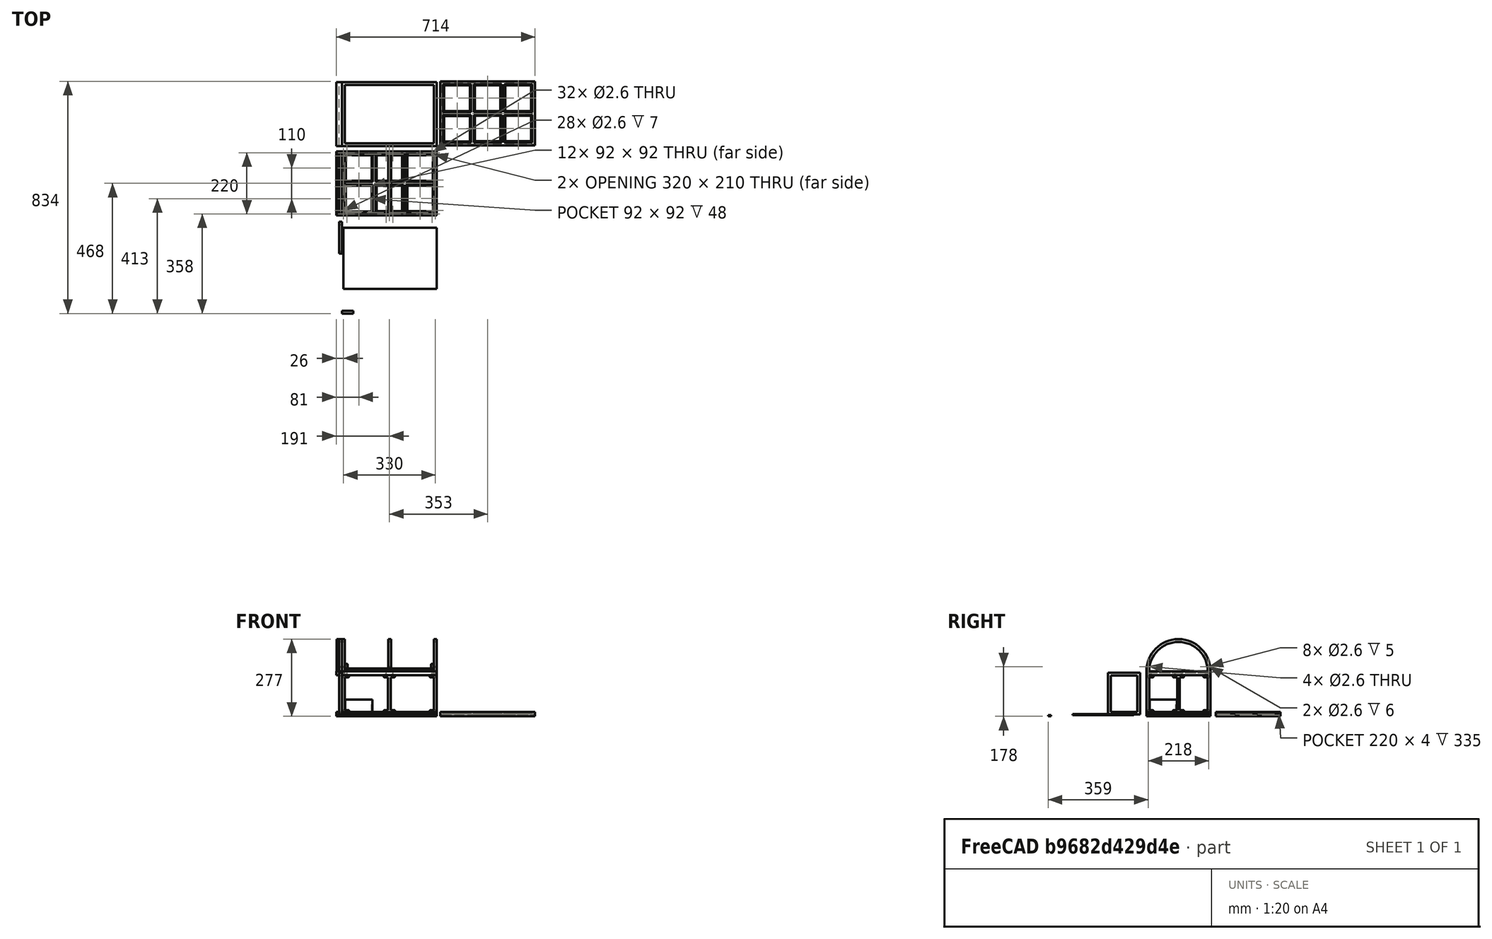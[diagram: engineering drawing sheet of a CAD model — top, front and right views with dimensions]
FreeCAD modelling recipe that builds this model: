
FCSTD DOCUMENT  (FreeCAD 0.18R4 (GitTag))
Label: 3DMODEL
License: All rights reserved
LicenseURL: http://en.wikipedia.org/wiki/All_rights_reserved
objects: Part::Box×95, Part::Cut×92, Part::Cylinder×85, Part::MultiFuse×18, App::MeasureDistance×12, Part::Fillet×12, Mesh::Feature×2
note: 302 computed .brp shape members not serialized (recipe doc carries the construction recipe); baked Part::Feature solids carry a one-line shape summary decoded from their .brp

FEATURE [Part::Box] Box  label="base1"
  AttacherType = Attacher::AttachEngine3D
  Height = 15
  Length = 340
  Width = 10
FEATURE [Part::Box] Box001  label="base2"
  AttacherType = Attacher::AttachEngine3D
  Height = 15
  Length = 340
  Placement = pos=(0,220,0) rot=(0,0,1;0rad)
  Width = 10
FEATURE [Part::Box] Box002  label="ancho"
  AttacherType = Attacher::AttachEngine3D
  Height = 15
  Length = 10
  Placement = pos=(0,10,0) rot=(0,0,1;0rad)
  Width = 210
FEATURE [Part::Box] Box003  label="ancho001"
  AttacherType = Attacher::AttachEngine3D
  Height = 15
  Length = 10
  Placement = pos=(330,10,0) rot=(0,0,1;0rad)
  Width = 210
FEATURE [Part::Box] Box004  label="cajita1"
  AttacherType = Attacher::AttachEngine3D
  Height = 2
  Length = 320
  Placement = pos=(10,10,8) rot=(0,0,1;0rad)
  Width = 210
FEATURE [Part::Box] Box006  label="base003"
  AttacherType = Attacher::AttachEngine3D
  Height = 7
  Length = 340
  Placement = pos=(0,110,8) rot=(0,0,1;0rad)
  Width = 10
FEATURE [Part::Box] Box011  label="ancho002"
  AttacherType = Attacher::AttachEngine3D
  Height = 7
  Length = 10
  Placement = pos=(110,10,8) rot=(0,0,1;0rad)
  Width = 210
FEATURE [Part::Box] Box012  label="ancho003"
  AttacherType = Attacher::AttachEngine3D
  Height = 7
  Length = 10
  Placement = pos=(220,10,8) rot=(0,0,1;0rad)
  Width = 210
FEATURE [Part::Box] Box013  label="cajita007"
  AttacherType = Attacher::AttachEngine3D
  Height = 24
  Length = 92
  Placement = pos=(14,14,0) rot=(0,0,1;0rad)
  Width = 92
FEATURE [Part::MultiFuse] Fusion  label="base"
  Shapes = -> [Box011,Box012,Box006,Box003,Box002,Box001,Box]
FEATURE [Part::Box] Box015  label="cajita009"
  AttacherType = Attacher::AttachEngine3D
  Height = 4
  Length = 335
  Placement = pos=(5,5,4) rot=(0,0,1;0rad)
  Width = 220
FEATURE [Part::Box] Box016  label="plancha"
  AttacherType = Attacher::AttachEngine3D
  Height = 4
  Length = 335
  Placement = pos=(5,-265,4) rot=(0,0,1;0rad)
  Width = 220
FEATURE [Part::Cut] Cut
  Base = -> Fusion
  Tool = -> Box015
FEATURE [Part::MultiFuse] Fusion001
  Shapes = -> [Cut,Box004]
FEATURE [Part::Cut] Cut001
  Base = -> Fusion001
  Tool = -> Box013
FEATURE [Part::Box] Box017  label="cajita011"
  AttacherType = Attacher::AttachEngine3D
  Height = 24
  Length = 92
  Placement = pos=(124,15,0) rot=(0,0,1;0rad)
  Width = 92
FEATURE [Part::Cut] Cut002
  Base = -> Cut001
  Tool = -> Box017
FEATURE [Part::Box] Box018  label="cajita012"
  AttacherType = Attacher::AttachEngine3D
  Height = 24
  Length = 92
  Placement = pos=(234,15,0) rot=(0,0,1;0rad)
  Width = 92
FEATURE [Part::Cut] Cut003
  Base = -> Cut002
  Tool = -> Box018
FEATURE [Part::Box] Box019  label="cajita013"
  AttacherType = Attacher::AttachEngine3D
  Height = 24
  Length = 92
  Placement = pos=(234,124,0) rot=(0,0,1;0rad)
  Width = 92
FEATURE [Part::Cut] Cut004
  Base = -> Cut003
  Tool = -> Box019
FEATURE [Part::Box] Box020  label="cajita014"
  AttacherType = Attacher::AttachEngine3D
  Height = 24
  Length = 92
  Placement = pos=(124,124,0) rot=(0,0,1;0rad)
  Width = 92
FEATURE [Part::Cut] Cut005
  Base = -> Cut004
  Tool = -> Box020
FEATURE [Part::Box] Box021  label="cajita015"
  AttacherType = Attacher::AttachEngine3D
  Height = 24
  Length = 92
  Placement = pos=(14,124,0) rot=(0,0,1;0rad)
  Width = 92
FEATURE [Part::Cut] Cut006  label="base004"
  Base = -> Cut005
  Tool = -> Box021
FEATURE [Part::Box] Box022  label="Cubo"
  AttacherType = Attacher::AttachEngine3D
  Height = 50
  Length = 98
  Placement = pos=(11,11,0) rot=(0,0,1;0rad)
  Width = 98
FEATURE [Part::Box] Box023  label="Cubo001"
  AttacherType = Attacher::AttachEngine3D
  Height = 80
  Length = 92
  Placement = pos=(14,14,2) rot=(0,0,1;0rad)
  Width = 92
FEATURE [Part::Cut] Cut007  label="cajita"
  Base = -> Box022
  Placement = pos=(0,0,10) rot=(0,0,1;0rad)
  Tool = -> Box023
FEATURE [App::MeasureDistance] Distance  label="Distance: 340,00 mm"
  Distance = 340
  P1 = (0,230,15)
  P2 = (340,229.956,15)
FEATURE [Part::Box] Box024  label="Cubo002"
  AttacherType = Attacher::AttachEngine3D
  Height = 15
  Length = 10
  Placement = pos=(0,259,0) rot=(0,0,1;0rad)
  Width = 210
FEATURE [App::MeasureDistance] Distance001  label="Distance: 230,00 mm"
  Distance = 230
  P1 = (340,230,15)
  P2 = (340,0,15)
FEATURE [Part::Box] Box025  label="base005"
  AttacherType = Attacher::AttachEngine3D
  Height = 15
  Length = 340
  Width = 10
FEATURE [Part::Box] Box026  label="base006"
  AttacherType = Attacher::AttachEngine3D
  Height = 15
  Length = 340
  Placement = pos=(0,220,0) rot=(0,0,1;0rad)
  Width = 10
FEATURE [Part::Box] Box027  label="ancho004"
  AttacherType = Attacher::AttachEngine3D
  Height = 15
  Length = 10
  Placement = pos=(330,10,0) rot=(0,0,1;0rad)
  Width = 210
FEATURE [Part::Box] Box028  label="base007"
  AttacherType = Attacher::AttachEngine3D
  Height = 7
  Length = 340
  Placement = pos=(0,110,8) rot=(0,0,1;0rad)
  Width = 10
FEATURE [Part::Box] Box029  label="ancho005"
  AttacherType = Attacher::AttachEngine3D
  Height = 7
  Length = 10
  Placement = pos=(110,10,8) rot=(0,0,1;0rad)
  Width = 210
FEATURE [Part::Box] Box030  label="cajita016"
  AttacherType = Attacher::AttachEngine3D
  Height = 2
  Length = 320
  Placement = pos=(10,10,8) rot=(0,0,1;0rad)
  Width = 210
FEATURE [Part::Box] Box031  label="ancho006"
  AttacherType = Attacher::AttachEngine3D
  Height = 7
  Length = 10
  Placement = pos=(220,10,8) rot=(0,0,1;0rad)
  Width = 210
FEATURE [Part::Box] Box032  label="cajita017"
  AttacherType = Attacher::AttachEngine3D
  Height = 24
  Length = 92
  Placement = pos=(14,14,0) rot=(0,0,1;0rad)
  Width = 92
FEATURE [Part::Box] Box033  label="ancho007"
  AttacherType = Attacher::AttachEngine3D
  Height = 15
  Length = 10
  Placement = pos=(0,10,0) rot=(0,0,1;0rad)
  Width = 210
FEATURE [Part::MultiFuse] Fusion003  label="base009"
  Shapes = -> [Box029,Box031,Box028,Box027,Box033,Box026,Box025]
FEATURE [Part::Box] Box034  label="cajita018"
  AttacherType = Attacher::AttachEngine3D
  Height = 24
  Length = 92
  Placement = pos=(124,124,0) rot=(0,0,1;0rad)
  Width = 92
FEATURE [Part::Box] Box035  label="cajita019"
  AttacherType = Attacher::AttachEngine3D
  Height = 24
  Length = 92
  Placement = pos=(124,15,0) rot=(0,0,1;0rad)
  Width = 92
FEATURE [Part::Box] Box036  label="cajita020"
  AttacherType = Attacher::AttachEngine3D
  Height = 24
  Length = 92
  Placement = pos=(234,124,0) rot=(0,0,1;0rad)
  Width = 92
FEATURE [Part::Box] Box037  label="cajita021"
  AttacherType = Attacher::AttachEngine3D
  Height = 24
  Length = 92
  Placement = pos=(234,15,0) rot=(0,0,1;0rad)
  Width = 92
FEATURE [Part::Box] Box039  label="cajita023"
  AttacherType = Attacher::AttachEngine3D
  Height = 4
  Length = 335
  Placement = pos=(5,5,4) rot=(0,0,1;0rad)
  Width = 220
FEATURE [Part::Cut] Cut012
  Base = -> Fusion003
  Tool = -> Box039
FEATURE [Part::MultiFuse] Fusion002
  Shapes = -> [Cut012,Box030]
FEATURE [Part::Cut] Cut008
  Base = -> Fusion002
  Tool = -> Box032
FEATURE [Part::Cut] Cut009
  Base = -> Cut008
  Tool = -> Box035
FEATURE [Part::Cut] Cut014
  Base = -> Cut009
  Tool = -> Box037
FEATURE [Part::Cut] Cut010
  Base = -> Cut014
  Tool = -> Box036
FEATURE [Part::Cut] Cut011
  Base = -> Cut010
  Tool = -> Box034
FEATURE [Part::Box] Box038  label="cajita022"
  AttacherType = Attacher::AttachEngine3D
  Height = 24
  Length = 92
  Placement = pos=(14,124,0) rot=(0,0,1;0rad)
  Width = 92
FEATURE [Part::Cut] Cut013  label="BaseOriginal"
  Base = -> Cut011
  Placement = pos=(353,251,0) rot=(0,0,1;0rad)
  Tool = -> Box038
FEATURE [Part::Box] Box040  label="Cubo003"
  AttacherType = Attacher::AttachEngine3D
  Height = 15
  Length = 340
  Placement = pos=(0,249,0) rot=(0,0,1;0rad)
  Width = 10
FEATURE [Part::Box] Box041  label="Cubo004"
  AttacherType = Attacher::AttachEngine3D
  Height = 15
  Length = 10
  Placement = pos=(330,259,0) rot=(0,0,1;0rad)
  Width = 210
FEATURE [Part::Box] Box042  label="Cubo005"
  AttacherType = Attacher::AttachEngine3D
  Height = 15
  Length = 340
  Placement = pos=(0,469,0) rot=(0,0,1;0rad)
  Width = 10
FEATURE [Part::MultiFuse] Fusion004  label="techo"
  Shapes = -> [Box042,Box041,Box040,Box024]
FEATURE [App::MeasureDistance] Distance002  label="Distance: 340,00 mm001"
  Distance = 340
  P1 = (0,479,15)
  P2 = (340,479,15)
FEATURE [App::MeasureDistance] Distance003  label="Distance: 230,00 mm001"
  Distance = 230
  P1 = (339.999,479,15)
  P2 = (340,249,15)
FEATURE [App::MeasureDistance] Distance004  label="Distance: 100,00 mm"
  Distance = 100
  P1 = (330,219.999,15)
  P2 = (230,219.997,15)
FEATURE [Part::Box] Box043  label="Cubo006"
  AttacherType = Attacher::AttachEngine3D
  Height = 5
  Length = 21
  Placement = pos=(-21,0,0) rot=(0,0,1;0rad)
  Width = 230
FEATURE [Part::Box] Box044  label="Cubo007"
  AttacherType = Attacher::AttachEngine3D
  Height = 10
  Length = 10
  Placement = pos=(-21,0,5) rot=(0,0,1;0rad)
  Width = 230
FEATURE [Part::Box] Box045  label="Cubo008"
  AttacherType = Attacher::AttachEngine3D
  Height = 5
  Length = 21
  Placement = pos=(-21,249,10) rot=(0,0,1;0rad)
  Width = 230
FEATURE [Part::Box] Box046  label="Cubo009"
  AttacherType = Attacher::AttachEngine3D
  Height = 10
  Length = 10
  Placement = pos=(-21,249,0) rot=(0,0,1;0rad)
  Width = 230
FEATURE [App::MeasureDistance] Distance005  label="Distance: 11,00 mm"
  Distance = 11
  P1 = (0,0,15)
  P2 = (-11,0,15)
FEATURE [Part::Box] Box048  label="Cubo011"
  AttacherType = Attacher::AttachEngine3D
  Height = 130
  Length = 10
  Placement = pos=(-37,220,15) rot=(0,0,1;0rad)
  Width = 10
FEATURE [Part::Box] Box049  label="Cubo012"
  AttacherType = Attacher::AttachEngine3D
  Height = 130
  Length = 10
  Placement = pos=(-37,115,15) rot=(0,0,1;0rad)
  Width = 10
FEATURE [Part::Box] Box050  label="Cubo013"
  AttacherType = Attacher::AttachEngine3D
  Height = 10
  Length = 10
  Placement = pos=(-37,115,145) rot=(0,0,1;0rad)
  Width = 115
FEATURE [Part::Box] Box051  label="Cubo014"
  AttacherType = Attacher::AttachEngine3D
  Height = 10
  Length = 10
  Placement = pos=(-37,115,5) rot=(0,0,1;0rad)
  Width = 115
FEATURE [Part::MultiFuse] Fusion005
  Placement = pos=(0,-249,147) rot=(0,0,1;0rad)
  Shapes = -> [Box045,Box046,Fusion004]
FEATURE [Part::Box] Box052  label="Cubo015"
  AttacherType = Attacher::AttachEngine3D
  Height = 15
  Length = 340
  Placement = pos=(0,249,0) rot=(0,0,1;0rad)
  Width = 10
FEATURE [Part::Box] Box053  label="Cubo016"
  AttacherType = Attacher::AttachEngine3D
  Height = 15
  Length = 10
  Placement = pos=(330,259,0) rot=(0,0,1;0rad)
  Width = 210
FEATURE [Part::Box] Box054  label="Cubo017"
  AttacherType = Attacher::AttachEngine3D
  Height = 15
  Length = 10
  Placement = pos=(0,259,0) rot=(0,0,1;0rad)
  Width = 210
FEATURE [Part::Box] Box055  label="Cubo018"
  AttacherType = Attacher::AttachEngine3D
  Height = 15
  Length = 340
  Placement = pos=(0,469,0) rot=(0,0,1;0rad)
  Width = 10
FEATURE [Part::MultiFuse] Fusion006  label="techo001"
  Shapes = -> [Box055,Box053,Box052,Box054]
FEATURE [Part::Box] Box056  label="Cubo019"
  AttacherType = Attacher::AttachEngine3D
  Height = 5
  Length = 21
  Placement = pos=(-21,249,10) rot=(0,0,1;0rad)
  Width = 230
FEATURE [Part::Box] Box057  label="Cubo020"
  AttacherType = Attacher::AttachEngine3D
  Height = 10
  Length = 10
  Placement = pos=(-21,249,0) rot=(0,0,1;0rad)
  Width = 230
FEATURE [Part::MultiFuse] Fusion007
  Placement = pos=(26.5,-253,1) rot=(0,0,1;0rad)
  Shapes = -> [Box048,Box049,Box050,Box051]
FEATURE [Mesh::Feature] GuiaE
  Placement = pos=(22.156,173,156) rot=(0,1,0;3.14159rad)
FEATURE [Mesh::Feature] EjeE
  Placement = pos=(-7.5,222.361,57.2209) rot=(0.069587,0.995146,0.069587;1.57566rad)
FEATURE [App::MeasureDistance] Distance006  label="Distance: 132,00 mm"
  Distance = 132
  P1 = (0,0,147)
  P2 = (0,0,15)
FEATURE [Part::Box] Box062  label="Cubo025"
  AttacherType = Attacher::AttachEngine3D
  Height = 7
  Length = 10
  Placement = pos=(0,10,140) rot=(0,0,1;0rad)
  Width = 15
FEATURE [Part::Box] Box063  label="Cubo026"
  AttacherType = Attacher::AttachEngine3D
  Height = 132
  Length = 10
  Placement = pos=(0,0,15) rot=(0,0,1;0rad)
  Width = 10
FEATURE [Part::Box] Box064  label="Cubo027"
  AttacherType = Attacher::AttachEngine3D
  Height = 7
  Length = 15
  Placement = pos=(10,0,140) rot=(0,0,1;0rad)
  Width = 10
FEATURE [Part::Box] Box065  label="Cubo028"
  AttacherType = Attacher::AttachEngine3D
  Height = 7
  Length = 15
  Placement = pos=(10,0,15) rot=(0,0,1;0rad)
  Width = 10
FEATURE [Part::Box] Box066  label="Cubo029"
  AttacherType = Attacher::AttachEngine3D
  Height = 7
  Length = 10
  Placement = pos=(0,10,15) rot=(0,0,1;0rad)
  Width = 15
FEATURE [Part::MultiFuse] Fusion008
  Shapes = -> [Box065,Box063,Box064,Box066,Box062]
FEATURE [Part::Box] Box067  label="Cubo030"
  AttacherType = Attacher::AttachEngine3D
  Height = 7
  Length = 15
  Placement = pos=(175,0,15) rot=(0,0,1;0rad)
  Width = 10
FEATURE [Part::Box] Box068  label="Cubo031"
  AttacherType = Attacher::AttachEngine3D
  Height = 132
  Length = 10
  Placement = pos=(165,0,15) rot=(0,0,1;0rad)
  Width = 10
FEATURE [Part::Box] Box069  label="Cubo032"
  AttacherType = Attacher::AttachEngine3D
  Height = 7
  Length = 15
  Placement = pos=(175,0,140) rot=(0,0,1;0rad)
  Width = 10
FEATURE [Part::Box] Box070  label="Cubo033"
  AttacherType = Attacher::AttachEngine3D
  Height = 7
  Length = 15
  Placement = pos=(150,0,15) rot=(0,0,1;0rad)
  Width = 10
FEATURE [Part::Box] Box071  label="Cubo034"
  AttacherType = Attacher::AttachEngine3D
  Height = 7
  Length = 15
  Placement = pos=(150,0,140) rot=(0,0,1;0rad)
  Width = 10
FEATURE [Part::MultiFuse] Fusion009
  Shapes = -> [Box069,Box067,Box068,Box070,Box071]
FEATURE [Part::Fillet] Fillet  label="Pilar_Esquina"
  Base = -> Fusion008
  Edges = 4 edges r=2: [Edge2,Edge35,Edge39,Edge52]
FEATURE [Part::Fillet] Fillet001  label="Pilar_Central"
  Base = -> Fusion009
  Edges = 4 edges r=2: [Edge4,Edge52,Edge55,Edge56]
FEATURE [Part::Cylinder] Cylinder  label="Cilindro"
  Angle = 360
  AttacherType = Attacher::AttachEngine3D
  Height = 146
  Placement = pos=(17,5,8) rot=(0,0,1;0rad)
  Radius = 1.3
FEATURE [App::MeasureDistance] Distance007  label="Distance: 22,01 mm"
  Distance = 22.006
  P1 = (10.0981,0,22)
  P2 = (9.58389,0,0)
FEATURE [App::MeasureDistance] Distance008  label="Distance: 7,00 mm"
  Distance = 7
  P1 = (10.043,0,22)
  P2 = (10.0386,0,15)
FEATURE [Part::Cylinder] Cylinder001  label="Cilindro001"
  Angle = 360
  AttacherType = Attacher::AttachEngine3D
  Height = 146
  Placement = pos=(17,5,8) rot=(0,0,1;0rad)
  Radius = 1.3
FEATURE [Part::Cut] Cut015
  Base = -> Fillet
  Tool = -> Cylinder
FEATURE [Part::Cut] Cut016
  Base = -> Fusion005
  Tool = -> Cylinder001
FEATURE [Part::Cylinder] Cylinder002  label="Cilindro002"
  Angle = 360
  AttacherType = Attacher::AttachEngine3D
  Height = 146
  Placement = pos=(5,17,8) rot=(0,0,1;0rad)
  Radius = 1.3
FEATURE [Part::Cut] Cut017
  Base = -> Cut016
  Tool = -> Cylinder002
FEATURE [Part::Cylinder] Cylinder004  label="Cilindro004"
  Angle = 360
  AttacherType = Attacher::AttachEngine3D
  Height = 146
  Placement = pos=(5,17,8) rot=(0,0,1;0rad)
  Radius = 1.3
FEATURE [Part::Cut] Cut018  label="Pilar001"
  Base = -> Cut015
  Tool = -> Cylinder004
FEATURE [Part::Cylinder] Cylinder005  label="Cilindro005"
  Angle = 360
  AttacherType = Attacher::AttachEngine3D
  Height = 146
  Placement = pos=(5,17,8) rot=(0,0,1;0rad)
  Radius = 1.3
FEATURE [Part::Cut] Cut019
  Base = -> Cut006
  Tool = -> Cylinder005
FEATURE [Part::Cylinder] Cylinder003  label="Cilindro003"
  Angle = 360
  AttacherType = Attacher::AttachEngine3D
  Height = 146
  Placement = pos=(17,5,8) rot=(0,0,1;0rad)
  Radius = 1.3
FEATURE [Part::Cut] Cut020
  Base = -> Cut019
  Tool = -> Cylinder003
FEATURE [Part::Cylinder] Cylinder006  label="Cilindro006"
  Angle = 360
  AttacherType = Attacher::AttachEngine3D
  Height = 146
  Placement = pos=(182,5,8) rot=(0,0,1;0rad)
  Radius = 1.3
FEATURE [Part::Cylinder] Cylinder007  label="Cilindro007"
  Angle = 360
  AttacherType = Attacher::AttachEngine3D
  Height = 146
  Placement = pos=(158,5,8) rot=(0,0,1;0rad)
  Radius = 1.3
FEATURE [Part::Cut] Cut021
  Base = -> Cut020
  Tool = -> Cylinder007
FEATURE [Part::Cylinder] Cylinder008  label="Cilindro008"
  Angle = 360
  AttacherType = Attacher::AttachEngine3D
  Height = 146
  Placement = pos=(158,5,8) rot=(0,0,1;0rad)
  Radius = 1.3
FEATURE [Part::Cut] Cut022
  Base = -> Fillet001
  Tool = -> Cylinder008
FEATURE [Part::Cylinder] Cylinder009  label="Cilindro009"
  Angle = 360
  AttacherType = Attacher::AttachEngine3D
  Height = 146
  Placement = pos=(158,5,8) rot=(0,0,1;0rad)
  Radius = 1.3
FEATURE [Part::Cut] Cut023
  Base = -> Cut017
  Tool = -> Cylinder009
FEATURE [Part::Cut] Cut024
  Base = -> Cut021
  Tool = -> Cylinder006
FEATURE [Part::Cylinder] Cylinder010  label="Cilindro010"
  Angle = 360
  AttacherType = Attacher::AttachEngine3D
  Height = 146
  Placement = pos=(182,5,8) rot=(0,0,1;0rad)
  Radius = 1.3
FEATURE [Part::Cut] Cut025  label="Pilar002"
  Base = -> Cut022
  Tool = -> Cylinder010
FEATURE [Part::Cylinder] Cylinder011  label="Cilindro011"
  Angle = 360
  AttacherType = Attacher::AttachEngine3D
  Height = 146
  Placement = pos=(182,5,8) rot=(0,0,1;0rad)
  Radius = 1.3
FEATURE [Part::Cut] Cut026
  Base = -> Cut023
  Tool = -> Cylinder011
FEATURE [Part::Cylinder] Cylinder012  label="Cilindro012"
  Angle = 360
  AttacherType = Attacher::AttachEngine3D
  Height = 146
  Placement = pos=(323,5,8) rot=(0,0,1;0rad)
  Radius = 1.3
FEATURE [Part::Box] Box072  label="Cubo035"
  AttacherType = Attacher::AttachEngine3D
  Height = 132
  Length = 10
  Placement = pos=(0,0,15) rot=(0,0,1;0rad)
  Width = 10
FEATURE [Part::Cylinder] Cylinder013  label="Cilindro013"
  Angle = 360
  AttacherType = Attacher::AttachEngine3D
  Height = 146
  Placement = pos=(17,5,8) rot=(0,0,1;0rad)
  Radius = 1.3
FEATURE [Part::Box] Box073  label="Cubo036"
  AttacherType = Attacher::AttachEngine3D
  Height = 7
  Length = 15
  Placement = pos=(10,0,15) rot=(0,0,1;0rad)
  Width = 10
FEATURE [Part::Box] Box074  label="Cubo037"
  AttacherType = Attacher::AttachEngine3D
  Height = 7
  Length = 10
  Placement = pos=(0,10,15) rot=(0,0,1;0rad)
  Width = 15
FEATURE [Part::Box] Box075  label="Cubo038"
  AttacherType = Attacher::AttachEngine3D
  Height = 7
  Length = 10
  Placement = pos=(0,10,140) rot=(0,0,1;0rad)
  Width = 15
FEATURE [Part::Cylinder] Cylinder014  label="Cilindro014"
  Angle = 360
  AttacherType = Attacher::AttachEngine3D
  Height = 146
  Placement = pos=(5,17,8) rot=(0,0,1;0rad)
  Radius = 1.3
FEATURE [Part::Box] Box076  label="Cubo039"
  AttacherType = Attacher::AttachEngine3D
  Height = 7
  Length = 15
  Placement = pos=(10,0,140) rot=(0,0,1;0rad)
  Width = 10
FEATURE [Part::MultiFuse] Fusion010
  Shapes = -> [Box073,Box072,Box076,Box074,Box075]
FEATURE [Part::Fillet] Fillet002  label="Pilar_Esquina001"
  Base = -> Fusion010
  Edges = 4 edges r=2: [Edge2,Edge35,Edge39,Edge52]
FEATURE [Part::Cut] Cut028
  Base = -> Fillet002
  Tool = -> Cylinder013
FEATURE [Part::Cut] Cut027  label="Pilar003"
  Base = -> Cut028
  Placement = pos=(340,0,0) rot=(0,0,1;1.5708rad)
  Tool = -> Cylinder014
FEATURE [Part::Cut] Cut029
  Base = -> Cut026
  Tool = -> Cylinder012
FEATURE [Part::Cylinder] Cylinder015  label="Cilindro015"
  Angle = 360
  AttacherType = Attacher::AttachEngine3D
  Height = 146
  Placement = pos=(323,5,8) rot=(0,0,1;0rad)
  Radius = 1.3
FEATURE [Part::Cut] Cut030
  Base = -> Cut024
  Tool = -> Cylinder015
FEATURE [Part::Cylinder] Cylinder016  label="Cilindro016"
  Angle = 360
  AttacherType = Attacher::AttachEngine3D
  Height = 146
  Placement = pos=(335,17,8) rot=(0,0,1;0rad)
  Radius = 1.3
FEATURE [Part::Cut] Cut031
  Base = -> Cut030
  Tool = -> Cylinder016
FEATURE [Part::Cylinder] Cylinder017  label="Cilindro017"
  Angle = 360
  AttacherType = Attacher::AttachEngine3D
  Height = 146
  Placement = pos=(335,17,8) rot=(0,0,1;0rad)
  Radius = 1.3
FEATURE [Part::Cut] Cut032
  Base = -> Cut029
  Tool = -> Cylinder017
FEATURE [Part::Cylinder] Cylinder018  label="Cilindro018"
  Angle = 360
  AttacherType = Attacher::AttachEngine3D
  Height = 146
  Placement = pos=(335,103,8) rot=(0,0,1;0rad)
  Radius = 1.3
FEATURE [Part::Cylinder] Cylinder019  label="Cilindro019"
  Angle = 360
  AttacherType = Attacher::AttachEngine3D
  Height = 146
  Placement = pos=(158,5,8) rot=(0,0,1;0rad)
  Radius = 1.3
FEATURE [Part::Cylinder] Cylinder020  label="Cilindro020"
  Angle = 360
  AttacherType = Attacher::AttachEngine3D
  Height = 146
  Placement = pos=(182,5,8) rot=(0,0,1;0rad)
  Radius = 1.3
FEATURE [Part::Box] Box077  label="Cubo040"
  AttacherType = Attacher::AttachEngine3D
  Height = 7
  Length = 15
  Placement = pos=(175,0,140) rot=(0,0,1;0rad)
  Width = 10
FEATURE [Part::Box] Box078  label="Cubo041"
  AttacherType = Attacher::AttachEngine3D
  Height = 7
  Length = 15
  Placement = pos=(150,0,140) rot=(0,0,1;0rad)
  Width = 10
FEATURE [Part::Box] Box079  label="Cubo042"
  AttacherType = Attacher::AttachEngine3D
  Height = 7
  Length = 15
  Placement = pos=(175,0,15) rot=(0,0,1;0rad)
  Width = 10
FEATURE [Part::Box] Box080  label="Cubo043"
  AttacherType = Attacher::AttachEngine3D
  Height = 132
  Length = 10
  Placement = pos=(165,0,15) rot=(0,0,1;0rad)
  Width = 10
FEATURE [Part::Box] Box081  label="Cubo044"
  AttacherType = Attacher::AttachEngine3D
  Height = 7
  Length = 15
  Placement = pos=(150,0,15) rot=(0,0,1;0rad)
  Width = 10
FEATURE [Part::MultiFuse] Fusion011
  Shapes = -> [Box077,Box079,Box080,Box081,Box078]
FEATURE [Part::Fillet] Fillet003  label="Pilar_Central001"
  Base = -> Fusion011
  Edges = 4 edges r=2: [Edge4,Edge52,Edge55,Edge56]
FEATURE [Part::Cut] Cut034
  Base = -> Fillet003
  Tool = -> Cylinder019
FEATURE [Part::Cut] Cut033  label="Pilar004"
  Base = -> Cut034
  Placement = pos=(340,-55,0) rot=(0,0,1;1.5708rad)
  Tool = -> Cylinder020
FEATURE [Part::Cylinder] Cylinder021  label="Cilindro021"
  Angle = 360
  AttacherType = Attacher::AttachEngine3D
  Height = 146
  Placement = pos=(5,17,8) rot=(0,0,1;0rad)
  Radius = 1.3
FEATURE [Part::Box] Box082  label="Cubo045"
  AttacherType = Attacher::AttachEngine3D
  Height = 7
  Length = 10
  Placement = pos=(0,10,140) rot=(0,0,1;0rad)
  Width = 15
FEATURE [Part::Cylinder] Cylinder022  label="Cilindro022"
  Angle = 360
  AttacherType = Attacher::AttachEngine3D
  Height = 146
  Placement = pos=(17,5,8) rot=(0,0,1;0rad)
  Radius = 1.3
FEATURE [Part::Box] Box083  label="Cubo046"
  AttacherType = Attacher::AttachEngine3D
  Height = 7
  Length = 15
  Placement = pos=(10,0,15) rot=(0,0,1;0rad)
  Width = 10
FEATURE [Part::Box] Box084  label="Cubo047"
  AttacherType = Attacher::AttachEngine3D
  Height = 7
  Length = 10
  Placement = pos=(0,10,15) rot=(0,0,1;0rad)
  Width = 15
FEATURE [Part::Box] Box085  label="Cubo048"
  AttacherType = Attacher::AttachEngine3D
  Height = 132
  Length = 10
  Placement = pos=(0,0,15) rot=(0,0,1;0rad)
  Width = 10
FEATURE [Part::Box] Box086  label="Cubo049"
  AttacherType = Attacher::AttachEngine3D
  Height = 7
  Length = 15
  Placement = pos=(10,0,140) rot=(0,0,1;0rad)
  Width = 10
FEATURE [Part::MultiFuse] Fusion012
  Shapes = -> [Box083,Box085,Box086,Box084,Box082]
FEATURE [Part::Fillet] Fillet004  label="Pilar_Esquina002"
  Base = -> Fusion012
  Edges = 4 edges r=2: [Edge2,Edge35,Edge39,Edge52]
FEATURE [Part::Cut] Cut036
  Base = -> Fillet004
  Tool = -> Cylinder022
FEATURE [Part::Cut] Cut035  label="Pilar005"
  Base = -> Cut036
  Placement = pos=(340,230,0) rot=(0,0,1;3.14159rad)
  Tool = -> Cylinder021
FEATURE [Part::Cylinder] Cylinder023  label="Cilindro023"
  Angle = 360
  AttacherType = Attacher::AttachEngine3D
  Height = 146
  Placement = pos=(158,5,8) rot=(0,0,1;0rad)
  Radius = 1.3
FEATURE [Part::Cylinder] Cylinder024  label="Cilindro024"
  Angle = 360
  AttacherType = Attacher::AttachEngine3D
  Height = 146
  Placement = pos=(182,5,8) rot=(0,0,1;0rad)
  Radius = 1.3
FEATURE [Part::Box] Box087  label="Cubo050"
  AttacherType = Attacher::AttachEngine3D
  Height = 7
  Length = 15
  Placement = pos=(175,0,140) rot=(0,0,1;0rad)
  Width = 10
FEATURE [Part::Box] Box088  label="Cubo051"
  AttacherType = Attacher::AttachEngine3D
  Height = 7
  Length = 15
  Placement = pos=(150,0,140) rot=(0,0,1;0rad)
  Width = 10
FEATURE [Part::Box] Box089  label="Cubo052"
  AttacherType = Attacher::AttachEngine3D
  Height = 7
  Length = 15
  Placement = pos=(175,0,15) rot=(0,0,1;0rad)
  Width = 10
FEATURE [Part::Box] Box090  label="Cubo053"
  AttacherType = Attacher::AttachEngine3D
  Height = 132
  Length = 10
  Placement = pos=(165,0,15) rot=(0,0,1;0rad)
  Width = 10
FEATURE [Part::Box] Box091  label="Cubo054"
  AttacherType = Attacher::AttachEngine3D
  Height = 7
  Length = 15
  Placement = pos=(150,0,15) rot=(0,0,1;0rad)
  Width = 10
FEATURE [Part::MultiFuse] Fusion013
  Shapes = -> [Box087,Box089,Box090,Box091,Box088]
FEATURE [Part::Fillet] Fillet005  label="Pilar_Central002"
  Base = -> Fusion013
  Edges = 4 edges r=2: [Edge4,Edge52,Edge55,Edge56]
FEATURE [Part::Cut] Cut038
  Base = -> Fillet005
  Tool = -> Cylinder023
FEATURE [Part::Cut] Cut037  label="Pilar006"
  Base = -> Cut038
  Placement = pos=(0,220,0) rot=(0,0,1;0rad)
  Tool = -> Cylinder024
FEATURE [Part::Cylinder] Cylinder025  label="Cilindro025"
  Angle = 360
  AttacherType = Attacher::AttachEngine3D
  Height = 146
  Placement = pos=(5,17,8) rot=(0,0,1;0rad)
  Radius = 1.3
FEATURE [Part::Box] Box092  label="Cubo055"
  AttacherType = Attacher::AttachEngine3D
  Height = 132
  Length = 10
  Placement = pos=(0,0,15) rot=(0,0,1;0rad)
  Width = 10
FEATURE [Part::Box] Box093  label="Cubo056"
  AttacherType = Attacher::AttachEngine3D
  Height = 7
  Length = 15
  Placement = pos=(10,0,15) rot=(0,0,1;0rad)
  Width = 10
FEATURE [Part::Cylinder] Cylinder026  label="Cilindro026"
  Angle = 360
  AttacherType = Attacher::AttachEngine3D
  Height = 146
  Placement = pos=(17,5,8) rot=(0,0,1;0rad)
  Radius = 1.3
FEATURE [Part::Box] Box094  label="Cubo057"
  AttacherType = Attacher::AttachEngine3D
  Height = 7
  Length = 10
  Placement = pos=(0,10,140) rot=(0,0,1;0rad)
  Width = 15
FEATURE [Part::Box] Box095  label="Cubo058"
  AttacherType = Attacher::AttachEngine3D
  Height = 7
  Length = 10
  Placement = pos=(0,10,15) rot=(0,0,1;0rad)
  Width = 15
FEATURE [Part::Box] Box096  label="Cubo059"
  AttacherType = Attacher::AttachEngine3D
  Height = 7
  Length = 15
  Placement = pos=(10,0,140) rot=(0,0,1;0rad)
  Width = 10
FEATURE [Part::MultiFuse] Fusion014
  Shapes = -> [Box093,Box092,Box096,Box095,Box094]
FEATURE [Part::Fillet] Fillet006  label="Pilar_Esquina003"
  Base = -> Fusion014
  Edges = 4 edges r=2: [Edge2,Edge35,Edge39,Edge52]
FEATURE [Part::Cut] Cut040
  Base = -> Fillet006
  Tool = -> Cylinder026
FEATURE [Part::Cut] Cut039  label="Pilar007"
  Base = -> Cut040
  Placement = pos=(0,230,0) rot=(0,0,-1;1.5708rad)
  Tool = -> Cylinder025
FEATURE [Part::Box] Box097  label="Cubo060"
  AttacherType = Attacher::AttachEngine3D
  Height = 7
  Length = 15
  Placement = pos=(150,0,140) rot=(0,0,1;0rad)
  Width = 10
FEATURE [Part::Cylinder] Cylinder027  label="Cilindro027"
  Angle = 360
  AttacherType = Attacher::AttachEngine3D
  Height = 146
  Placement = pos=(158,5,8) rot=(0,0,1;0rad)
  Radius = 1.3
FEATURE [Part::Box] Box098  label="Cubo061"
  AttacherType = Attacher::AttachEngine3D
  Height = 7
  Length = 15
  Placement = pos=(150,0,15) rot=(0,0,1;0rad)
  Width = 10
FEATURE [Part::Cylinder] Cylinder028  label="Cilindro028"
  Angle = 360
  AttacherType = Attacher::AttachEngine3D
  Height = 146
  Placement = pos=(182,5,8) rot=(0,0,1;0rad)
  Radius = 1.3
FEATURE [Part::Box] Box099  label="Cubo062"
  AttacherType = Attacher::AttachEngine3D
  Height = 7
  Length = 15
  Placement = pos=(175,0,140) rot=(0,0,1;0rad)
  Width = 10
FEATURE [Part::Box] Box100  label="Cubo063"
  AttacherType = Attacher::AttachEngine3D
  Height = 7
  Length = 15
  Placement = pos=(175,0,15) rot=(0,0,1;0rad)
  Width = 10
FEATURE [Part::Box] Box101  label="Cubo064"
  AttacherType = Attacher::AttachEngine3D
  Height = 132
  Length = 10
  Placement = pos=(165,0,15) rot=(0,0,1;0rad)
  Width = 10
FEATURE [Part::MultiFuse] Fusion015
  Shapes = -> [Box099,Box100,Box101,Box098,Box097]
FEATURE [Part::Fillet] Fillet007  label="Pilar_Central003"
  Base = -> Fusion015
  Edges = 4 edges r=2: [Edge4,Edge52,Edge55,Edge56]
FEATURE [Part::Cut] Cut041
  Base = -> Fillet007
  Tool = -> Cylinder027
FEATURE [Part::Cut] Cut042  label="Pilar008"
  Base = -> Cut041
  Placement = pos=(10,-55,0) rot=(0,0,1;1.5708rad)
  Tool = -> Cylinder028
FEATURE [Part::Cut] Cut043
  Base = -> Cut032
  Tool = -> Cylinder018
FEATURE [Part::Cylinder] Cylinder029  label="Cilindro029"
  Angle = 360
  AttacherType = Attacher::AttachEngine3D
  Height = 146
  Placement = pos=(335,103,8) rot=(0,0,1;0rad)
  Radius = 1.3
FEATURE [Part::Cut] Cut044
  Base = -> Cut031
  Tool = -> Cylinder029
FEATURE [Part::Cylinder] Cylinder030  label="Cilindro030"
  Angle = 360
  AttacherType = Attacher::AttachEngine3D
  Height = 146
  Placement = pos=(335,127,8) rot=(0,0,1;0rad)
  Radius = 1.3
FEATURE [Part::Cut] Cut045
  Base = -> Cut043
  Tool = -> Cylinder030
FEATURE [Part::Cylinder] Cylinder031  label="Cilindro031"
  Angle = 360
  AttacherType = Attacher::AttachEngine3D
  Height = 146
  Placement = pos=(335,127,8) rot=(0,0,1;0rad)
  Radius = 1.3
FEATURE [Part::Cut] Cut046
  Base = -> Cut044
  Tool = -> Cylinder031
FEATURE [Part::Cylinder] Cylinder032  label="Cilindro032"
  Angle = 360
  AttacherType = Attacher::AttachEngine3D
  Height = 146
  Placement = pos=(335,213,8) rot=(0,0,1;0rad)
  Radius = 1.3
FEATURE [Part::Cut] Cut047
  Base = -> Cut045
  Tool = -> Cylinder032
FEATURE [Part::Cylinder] Cylinder033  label="Cilindro033"
  Angle = 360
  AttacherType = Attacher::AttachEngine3D
  Height = 146
  Placement = pos=(335,213,8) rot=(0,0,1;0rad)
  Radius = 1.3
FEATURE [Part::Cut] Cut048
  Base = -> Cut046
  Tool = -> Cylinder033
FEATURE [Part::Cylinder] Cylinder034  label="Cilindro034"
  Angle = 360
  AttacherType = Attacher::AttachEngine3D
  Height = 146
  Placement = pos=(323,225,8) rot=(0,0,1;0rad)
  Radius = 1.3
FEATURE [Part::Cut] Cut049
  Base = -> Cut047
  Tool = -> Cylinder034
FEATURE [Part::Cylinder] Cylinder035  label="Cilindro035"
  Angle = 360
  AttacherType = Attacher::AttachEngine3D
  Height = 146
  Placement = pos=(323,225,8) rot=(0,0,1;0rad)
  Radius = 1.3
FEATURE [Part::Cut] Cut050
  Base = -> Cut048
  Tool = -> Cylinder035
FEATURE [Part::Cylinder] Cylinder036  label="Cilindro036"
  Angle = 360
  AttacherType = Attacher::AttachEngine3D
  Height = 146
  Placement = pos=(182,225,8) rot=(0,0,1;0rad)
  Radius = 1.3
FEATURE [Part::Cut] Cut051
  Base = -> Cut049
  Tool = -> Cylinder036
FEATURE [Part::Cylinder] Cylinder037  label="Cilindro037"
  Angle = 360
  AttacherType = Attacher::AttachEngine3D
  Height = 146
  Placement = pos=(182,225,8) rot=(0,0,1;0rad)
  Radius = 1.3
FEATURE [Part::Cut] Cut052
  Base = -> Cut050
  Tool = -> Cylinder037
FEATURE [Part::Cylinder] Cylinder038  label="Cilindro038"
  Angle = 360
  AttacherType = Attacher::AttachEngine3D
  Height = 146
  Placement = pos=(158,225,8) rot=(0,0,1;0rad)
  Radius = 1.3
FEATURE [Part::Cut] Cut053
  Base = -> Cut052
  Tool = -> Cylinder038
FEATURE [Part::Cylinder] Cylinder039  label="Cilindro039"
  Angle = 360
  AttacherType = Attacher::AttachEngine3D
  Height = 146
  Placement = pos=(158,225,8) rot=(0,0,1;0rad)
  Radius = 1.3
FEATURE [Part::Cut] Cut054
  Base = -> Cut051
  Tool = -> Cylinder039
FEATURE [Part::Cylinder] Cylinder040  label="Cilindro040"
  Angle = 360
  AttacherType = Attacher::AttachEngine3D
  Height = 146
  Placement = pos=(17,225,8) rot=(0,0,1;0rad)
  Radius = 1.3
FEATURE [Part::Cut] Cut055
  Base = -> Cut054
  Tool = -> Cylinder040
FEATURE [Part::Cylinder] Cylinder041  label="Cilindro041"
  Angle = 360
  AttacherType = Attacher::AttachEngine3D
  Height = 146
  Placement = pos=(17,225,8) rot=(0,0,1;0rad)
  Radius = 1.3
FEATURE [Part::Cut] Cut056
  Base = -> Cut053
  Tool = -> Cylinder041
FEATURE [Part::Cylinder] Cylinder042  label="Cilindro042"
  Angle = 360
  AttacherType = Attacher::AttachEngine3D
  Height = 146
  Placement = pos=(5,213,8) rot=(0,0,1;0rad)
  Radius = 1.3
FEATURE [Part::Cut] Cut057
  Base = -> Cut056
  Tool = -> Cylinder042
FEATURE [Part::Cylinder] Cylinder043  label="Cilindro043"
  Angle = 360
  AttacherType = Attacher::AttachEngine3D
  Height = 146
  Placement = pos=(5,213,8) rot=(0,0,1;0rad)
  Radius = 1.3
FEATURE [Part::Cut] Cut058
  Base = -> Cut055
  Tool = -> Cylinder043
FEATURE [Part::Cylinder] Cylinder044  label="Cilindro044"
  Angle = 360
  AttacherType = Attacher::AttachEngine3D
  Height = 146
  Placement = pos=(5,127,8) rot=(0,0,1;0rad)
  Radius = 1.3
FEATURE [Part::Cut] Cut059
  Base = -> Cut042
  Tool = -> Cylinder044
FEATURE [Part::Cylinder] Cylinder045  label="Cilindro045"
  Angle = 360
  AttacherType = Attacher::AttachEngine3D
  Height = 146
  Placement = pos=(5,127,8) rot=(0,0,1;0rad)
  Radius = 1.3
FEATURE [Part::Cut] Cut060
  Base = -> Cut058
  Tool = -> Cylinder045
FEATURE [Part::Cylinder] Cylinder046  label="Cilindro046"
  Angle = 360
  AttacherType = Attacher::AttachEngine3D
  Height = 146
  Placement = pos=(5,103,8) rot=(0,0,1;0rad)
  Radius = 1.3
FEATURE [Part::Cut] Cut061
  Base = -> Cut059
  Tool = -> Cylinder046
FEATURE [Part::Cylinder] Cylinder047  label="Cilindro047"
  Angle = 360
  AttacherType = Attacher::AttachEngine3D
  Height = 146
  Placement = pos=(5,103,8) rot=(0,0,1;0rad)
  Radius = 1.3
FEATURE [Part::Cut] Cut062
  Base = -> Cut060
  Tool = -> Cylinder047
FEATURE [Part::Cylinder] Cylinder048  label="Cilindro048"
  Angle = 360
  AttacherType = Attacher::AttachEngine3D
  Height = 146
  Placement = pos=(5,103,8) rot=(0,0,1;0rad)
  Radius = 1.3
FEATURE [Part::Cut] Cut063
  Base = -> Cut061
  Tool = -> Cylinder048
FEATURE [Part::Cylinder] Cylinder049  label="Cilindro049"
  Angle = 360
  AttacherType = Attacher::AttachEngine3D
  Height = 146
  Placement = pos=(5,127,8) rot=(0,0,1;0rad)
  Radius = 1.3
FEATURE [Part::Cut] Cut064
  Base = -> Cut057
  Tool = -> Cylinder049
FEATURE [Part::Cylinder] Cylinder050  label="Cilindro050"
  Angle = 360
  AttacherType = Attacher::AttachEngine3D
  Height = 146
  Placement = pos=(5,103,8) rot=(0,0,1;0rad)
  Radius = 1.3
FEATURE [Part::Cut] Cut065
  Base = -> Cut064
  Tool = -> Cylinder050
FEATURE [Part::Cylinder] Cylinder051  label="Cilindro051"
  Angle = 180
  AttacherType = Attacher::AttachEngine3D
  Height = 10
  Placement = pos=(-3,115,171) rot=(0.57735,-0.57735,-0.57735;2.0944rad)
  Radius = 115
FEATURE [Part::Cylinder] Cylinder052  label="Cilindro052"
  Angle = 180
  AttacherType = Attacher::AttachEngine3D
  Height = 10
  Placement = pos=(-3,115,171) rot=(0.57735,-0.57735,-0.57735;2.0944rad)
  Radius = 105
FEATURE [Part::Cut] Cut066
  Base = -> Cylinder051
  Placement = pos=(13,0,-9) rot=(0,0,1;0rad)
  Tool = -> Cylinder052
FEATURE [Part::Cylinder] Cylinder053  label="Cilindro053"
  Angle = 180
  AttacherType = Attacher::AttachEngine3D
  Height = 10
  Placement = pos=(-3,115,171) rot=(0.57735,-0.57735,-0.57735;2.0944rad)
  Radius = 115
FEATURE [Part::Cylinder] Cylinder054  label="Cilindro054"
  Angle = 180
  AttacherType = Attacher::AttachEngine3D
  Height = 10
  Placement = pos=(-3,115,171) rot=(0.57735,-0.57735,-0.57735;2.0944rad)
  Radius = 105
FEATURE [Part::Cut] Cut067
  Base = -> Cylinder053
  Placement = pos=(343,0,-9) rot=(0,0,1;0rad)
  Tool = -> Cylinder054
FEATURE [Part::Box] Box102  label="Cubo065"
  AttacherType = Attacher::AttachEngine3D
  Height = 10
  Length = 320
  Placement = pos=(10,0,162) rot=(0,0,1;0rad)
  Width = 10
FEATURE [Part::Cylinder] Cylinder055  label="Cilindro055"
  Angle = 13
  AttacherType = Attacher::AttachEngine3D
  Height = 10
  Placement = pos=(20,115,162) rot=(0.57735,-0.57735,-0.57735;2.0944rad)
  Radius = 115
FEATURE [Part::Cylinder] Cylinder056  label="Cilindro056"
  Angle = 13
  AttacherType = Attacher::AttachEngine3D
  Height = 10
  Placement = pos=(20,115,162) rot=(0.57735,-0.57735,-0.57735;2.0944rad)
  Radius = 105
FEATURE [Part::Cut] Cut068
  Base = -> Cylinder055
  Placement = pos=(310,0,0) rot=(0,0,1;0rad)
  Tool = -> Cylinder056
FEATURE [Part::Cylinder] Cylinder057  label="Cilindro057"
  Angle = 13
  AttacherType = Attacher::AttachEngine3D
  Height = 340
  Placement = pos=(340,115,162) rot=(0.57735,-0.57735,-0.57735;2.0944rad)
  Radius = 115
FEATURE [Part::Cylinder] Cylinder058  label="Cilindro058"
  Angle = 13
  AttacherType = Attacher::AttachEngine3D
  Height = 352
  Placement = pos=(340,115,162) rot=(0.57735,-0.57735,-0.57735;2.0944rad)
  Radius = 105
FEATURE [Part::Cut] Cut069
  Base = -> Cylinder057
  Placement = pos=(0,-10.1,0) rot=(0,0,1;0rad)
  Tool = -> Cylinder058
FEATURE [Part::Cut] Cut070
  Base = -> Box102
  Tool = -> Cut069
FEATURE [Part::Cylinder] Cylinder059  label="Cilindro059"
  Angle = 13
  AttacherType = Attacher::AttachEngine3D
  Height = 10
  Placement = pos=(20,115,162) rot=(0.57735,-0.57735,-0.57735;2.0944rad)
  Radius = 115
FEATURE [Part::Cylinder] Cylinder060  label="Cilindro060"
  Angle = 13
  AttacherType = Attacher::AttachEngine3D
  Height = 10
  Placement = pos=(20,115,162) rot=(0.57735,-0.57735,-0.57735;2.0944rad)
  Radius = 105
FEATURE [Part::Cut] Cut071
  Base = -> Cylinder059
  Tool = -> Cylinder060
FEATURE [Part::Fillet] Fillet008
  Base = -> Cut071
  Edges = 1 edges r=2: [Edge8]
FEATURE [Part::Fillet] Fillet009
  Base = -> Cut068
  Edges = 1 edges r=2: [Edge7]
FEATURE [Part::Cylinder] Cylinder061  label="Cilindro061"
  Angle = 360
  AttacherType = Attacher::AttachEngine3D
  Height = 331
  Placement = pos=(5,6,178) rot=(0,1,0;1.5708rad)
  Radius = 1.3
FEATURE [Part::MultiFuse] Fusion016
  Shapes = -> [Fillet009,Fillet008,Cut070]
FEATURE [Part::Cut] Cut072
  Base = -> Cut067
  Tool = -> Cylinder061
FEATURE [Part::Cylinder] Cylinder062  label="Cilindro062"
  Angle = 360
  AttacherType = Attacher::AttachEngine3D
  Height = 331
  Placement = pos=(5,6,178) rot=(0,1,0;1.5708rad)
  Radius = 1.3
FEATURE [Part::Cut] Cut073
  Base = -> Cut066
  Tool = -> Cylinder062
FEATURE [Part::Cylinder] Cylinder063  label="Cilindro063"
  Angle = 360
  AttacherType = Attacher::AttachEngine3D
  Height = 331
  Placement = pos=(5,6,178) rot=(0,1,0;1.5708rad)
  Radius = 1.3
FEATURE [Part::Cut] Cut074
  Base = -> Fusion016
  Placement = pos=(340,230,0) rot=(0,0,1;3.14159rad)
  Tool = -> Cylinder063
FEATURE [Part::Cylinder] Cylinder064  label="Cilindro064"
  Angle = 13
  AttacherType = Attacher::AttachEngine3D
  Height = 10
  Placement = pos=(20,115,162) rot=(0.57735,-0.57735,-0.57735;2.0944rad)
  Radius = 115
FEATURE [Part::Cylinder] Cylinder065  label="Cilindro065"
  Angle = 13
  AttacherType = Attacher::AttachEngine3D
  Height = 10
  Placement = pos=(20,115,162) rot=(0.57735,-0.57735,-0.57735;2.0944rad)
  Radius = 115
FEATURE [Part::Cylinder] Cylinder066  label="Cilindro066"
  Angle = 360
  AttacherType = Attacher::AttachEngine3D
  Height = 331
  Placement = pos=(5,6,178) rot=(0,1,0;1.5708rad)
  Radius = 1.3
FEATURE [Part::Box] Box103  label="Cubo066"
  AttacherType = Attacher::AttachEngine3D
  Height = 10
  Length = 320
  Placement = pos=(10,0,162) rot=(0,0,1;0rad)
  Width = 10
FEATURE [Part::Cylinder] Cylinder067  label="Cilindro067"
  Angle = 13
  AttacherType = Attacher::AttachEngine3D
  Height = 340
  Placement = pos=(340,115,162) rot=(0.57735,-0.57735,-0.57735;2.0944rad)
  Radius = 115
FEATURE [Part::Cylinder] Cylinder068  label="Cilindro068"
  Angle = 13
  AttacherType = Attacher::AttachEngine3D
  Height = 352
  Placement = pos=(340,115,162) rot=(0.57735,-0.57735,-0.57735;2.0944rad)
  Radius = 105
FEATURE [Part::Cut] Cut078
  Base = -> Cylinder067
  Placement = pos=(0,-10.1,0) rot=(0,0,1;0rad)
  Tool = -> Cylinder068
FEATURE [Part::Cut] Cut079
  Base = -> Box103
  Tool = -> Cut078
FEATURE [Part::Cylinder] Cylinder069  label="Cilindro069"
  Angle = 13
  AttacherType = Attacher::AttachEngine3D
  Height = 10
  Placement = pos=(20,115,162) rot=(0.57735,-0.57735,-0.57735;2.0944rad)
  Radius = 105
FEATURE [Part::Cut] Cut077
  Base = -> Cylinder064
  Placement = pos=(310,0,0) rot=(0,0,1;0rad)
  Tool = -> Cylinder069
FEATURE [Part::Fillet] Fillet010
  Base = -> Cut077
  Edges = 1 edges r=2: [Edge7]
FEATURE [Part::Cylinder] Cylinder070  label="Cilindro070"
  Angle = 13
  AttacherType = Attacher::AttachEngine3D
  Height = 10
  Placement = pos=(20,115,162) rot=(0.57735,-0.57735,-0.57735;2.0944rad)
  Radius = 105
FEATURE [Part::Cut] Cut075
  Base = -> Cylinder065
  Tool = -> Cylinder070
FEATURE [Part::Fillet] Fillet011
  Base = -> Cut075
  Edges = 1 edges r=2: [Edge8]
FEATURE [Part::MultiFuse] Fusion017
  Shapes = -> [Fillet010,Fillet011,Cut079]
FEATURE [Part::Cut] Cut076
  Base = -> Fusion017
  Tool = -> Cylinder066
FEATURE [Part::Cylinder] Cylinder071  label="Cilindro071"
  Angle = 360
  AttacherType = Attacher::AttachEngine3D
  Height = 331
  Placement = pos=(5,224,178) rot=(0,1,0;1.5708rad)
  Radius = 1.3
FEATURE [Part::Cut] Cut080
  Base = -> Cut073
  Tool = -> Cylinder071
FEATURE [Part::Cylinder] Cylinder072  label="Cilindro072"
  Angle = 360
  AttacherType = Attacher::AttachEngine3D
  Height = 331
  Placement = pos=(5,224,178) rot=(0,1,0;1.5708rad)
  Radius = 1.3
FEATURE [Part::Cut] Cut081
  Base = -> Cut072
  Tool = -> Cylinder072
FEATURE [Part::Box] Box104  label="Cubo067"
  AttacherType = Attacher::AttachEngine3D
  Height = 4
  Length = 40
  Placement = pos=(0,-353,0) rot=(0,0,1;0rad)
  Width = 10
FEATURE [App::MeasureDistance] Distance009  label="Distance: 40,00 mm"
  Distance = 40
  P1 = (150,0,15.0482)
  P2 = (190,0,15)
FEATURE [App::MeasureDistance] Distance010  label="Distance: 95,00 mm"
  Distance = 95
  P1 = (-10.5,-33,16)
  P2 = (-10.5,-128,16)
FEATURE [App::MeasureDistance] Distance011  label="Distance: 130,00 mm"
  Distance = 130
  P1 = (-10.5,-128,16)
  P2 = (-10.5,-128,146)
FEATURE [Part::Cylinder] Cylinder073  label="Cilindro073"
  Angle = 180
  AttacherType = Attacher::AttachEngine3D
  Height = 10
  Placement = pos=(-3,115,171) rot=(0.57735,-0.57735,-0.57735;2.0944rad)
  Radius = 115
FEATURE [Part::Cylinder] Cylinder074  label="Cilindro074"
  Angle = 180
  AttacherType = Attacher::AttachEngine3D
  Height = 10
  Placement = pos=(-3,115,171) rot=(0.57735,-0.57735,-0.57735;2.0944rad)
  Radius = 105
FEATURE [Part::Cut] Cut083
  Base = -> Cylinder073
  Placement = pos=(13,0,-9) rot=(0,0,1;0rad)
  Tool = -> Cylinder074
FEATURE [Part::Cylinder] Cylinder075  label="Cilindro075"
  Angle = 360
  AttacherType = Attacher::AttachEngine3D
  Height = 331
  Placement = pos=(5,6,178) rot=(0,1,0;1.5708rad)
  Radius = 1.3
FEATURE [Part::Cut] Cut084
  Base = -> Cut083
  Tool = -> Cylinder075
FEATURE [Part::Cylinder] Cylinder076  label="Cilindro076"
  Angle = 360
  AttacherType = Attacher::AttachEngine3D
  Height = 331
  Placement = pos=(5,224,178) rot=(0,1,0;1.5708rad)
  Radius = 1.3
FEATURE [Part::Cut] Cut082
  Base = -> Cut084
  Placement = pos=(-10,0,0) rot=(0,0,1;0rad)
  Tool = -> Cylinder076
FEATURE [Part::Cylinder] Cylinder077  label="Cilindro077"
  Angle = 180
  AttacherType = Attacher::AttachEngine3D
  Height = 10
  Placement = pos=(-3,115,171) rot=(0.57735,-0.57735,-0.57735;2.0944rad)
  Radius = 115
FEATURE [Part::Cylinder] Cylinder078  label="Cilindro078"
  Angle = 360
  AttacherType = Attacher::AttachEngine3D
  Height = 331
  Placement = pos=(5,6,178) rot=(0,1,0;1.5708rad)
  Radius = 1.3
FEATURE [Part::Cylinder] Cylinder079  label="Cilindro079"
  Angle = 180
  AttacherType = Attacher::AttachEngine3D
  Height = 10
  Placement = pos=(-3,115,171) rot=(0.57735,-0.57735,-0.57735;2.0944rad)
  Radius = 105
FEATURE [Part::Cylinder] Cylinder080  label="Cilindro080"
  Angle = 360
  AttacherType = Attacher::AttachEngine3D
  Height = 331
  Placement = pos=(5,224,178) rot=(0,1,0;1.5708rad)
  Radius = 1.3
FEATURE [Part::Cut] Cut086
  Base = -> Cylinder077
  Placement = pos=(13,0,-9) rot=(0,0,1;0rad)
  Tool = -> Cylinder079
FEATURE [Part::Cut] Cut087
  Base = -> Cut086
  Tool = -> Cylinder078
FEATURE [Part::Cut] Cut085
  Base = -> Cut087
  Placement = pos=(166,0,0) rot=(0,0,1;0rad)
  Tool = -> Cylinder080
FEATURE [Part::Cylinder] Cylinder081  label="Cilindro081"
  Angle = 180
  AttacherType = Attacher::AttachEngine3D
  Height = 10
  Placement = pos=(-3,115,171) rot=(0.57735,-0.57735,-0.57735;2.0944rad)
  Radius = 115
FEATURE [Part::Cylinder] Cylinder082  label="Cilindro082"
  Angle = 180
  AttacherType = Attacher::AttachEngine3D
  Height = 10
  Placement = pos=(-3,115,171) rot=(0.57735,-0.57735,-0.57735;2.0944rad)
  Radius = 105
FEATURE [Part::Cylinder] Cylinder083  label="Cilindro083"
  Angle = 360
  AttacherType = Attacher::AttachEngine3D
  Height = 331
  Placement = pos=(5,6,178) rot=(0,1,0;1.5708rad)
  Radius = 1.3
FEATURE [Part::Cylinder] Cylinder084  label="Cilindro084"
  Angle = 360
  AttacherType = Attacher::AttachEngine3D
  Height = 331
  Placement = pos=(5,224,178) rot=(0,1,0;1.5708rad)
  Radius = 1.3
FEATURE [Part::Cut] Cut089
  Base = -> Cylinder081
  Placement = pos=(13,0,-9) rot=(0,0,1;0rad)
  Tool = -> Cylinder082
FEATURE [Part::Cut] Cut090
  Base = -> Cut089
  Tool = -> Cylinder083
FEATURE [Part::Cut] Cut088
  Base = -> Cut090
  Placement = pos=(-20,0,0) rot=(0,0,1;0rad)
  Tool = -> Cylinder084
FEATURE [Part::Box] Box105  label="Cubo068"
  AttacherType = Attacher::AttachEngine3D
  Height = 10
  Length = 202
  Placement = pos=(0,0,162) rot=(0,0,1;0rad)
  Width = 239
FEATURE [Part::Cut] Cut091
  Base = -> Cut085
  Tool = -> Box105
